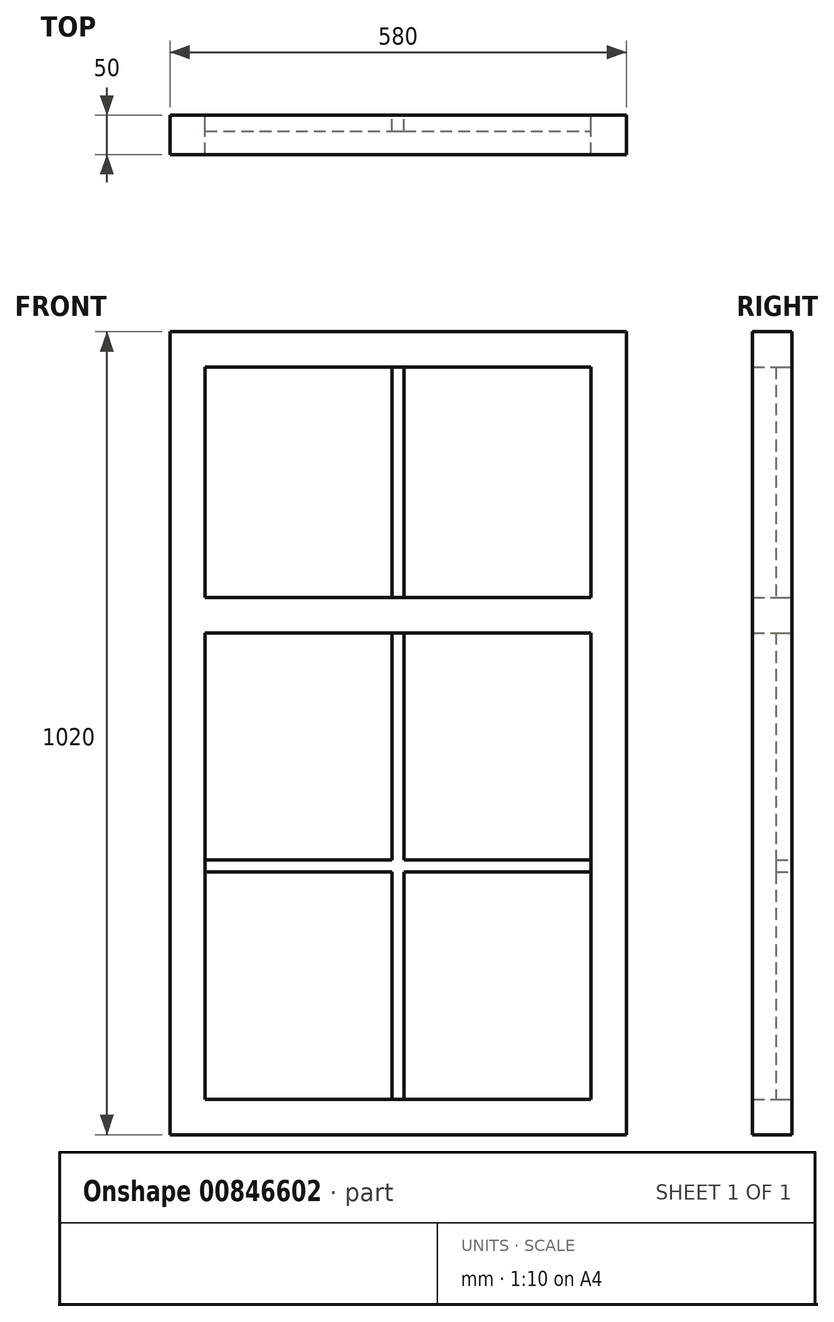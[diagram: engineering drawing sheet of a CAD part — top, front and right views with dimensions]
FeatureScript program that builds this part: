
annotation { "Feature Type Name" : "Feature", "Feature Type Description" : "" }
export const myFeature = defineFeature(function(context is Context, id is Id, definition is map)
    precondition{}
    {
        {
            var Q0;
            Q0=qCreatedBy(makeId("Front.planeOp"),FACE);
            var sketch = newSketch(context, id + "F0", { "sketchPlane" : qUnion([Q0])});
            skLineSegment(sketch, "E0.bottom", {"start": v(0, 0) * mm, "end": v(580, 0) * mm});
            skLineSegment(sketch, "E0.top", {"start": v(0, 1020) * mm, "end": v(580, 1020) * mm});
            skLineSegment(sketch, "E0.left", {"start": v(0, 0) * mm, "end": v(0, 1020) * mm});
            skLineSegment(sketch, "E0.right", {"start": v(580, 0) * mm, "end": v(580, 1020) * mm});
            skLineSegment(sketch, "E1.bottom", {"start": v(45, 975) * mm, "end": v(535, 975) * mm});
            skLineSegment(sketch, "E1.top", {"start": v(45, 45) * mm, "end": v(535, 45) * mm});
            skLineSegment(sketch, "E1.left", {"start": v(45, 975) * mm, "end": v(45, 682.5) * mm});
            skLineSegment(sketch, "E1.right", {"start": v(535, 975) * mm, "end": v(535, 682.5) * mm});
            skLineSegment(sketch, "E2.bottom", {"start": v(45, 682.5) * mm, "end": v(535, 682.5) * mm});
            skLineSegment(sketch, "E2.top", {"start": v(45, 637.5) * mm, "end": v(535, 637.5) * mm});
            skLineSegment(sketch, "E3.trimOffspring", {"start": v(535, 637.5) * mm, "end": v(535, 45) * mm});
            skLineSegment(sketch, "E4.trimOffspring", {"start": v(45, 637.5) * mm, "end": v(45, 45) * mm});
            skSolve(sketch);
        }
        {
            var Q0;
            Q0=qSketchRegion(id+"F0",true);
            extrude(context, id + "F1", {"entities" : qUnion([Q0]), "depth" : 50 * mm, "offsetDistance" : 25 * mm});
        }
        {
            var Q0;
            Q0=qCreatedBy(makeId("Front.planeOp"),FACE);
            var sketch = newSketch(context, id + "F2", { "sketchPlane" : qUnion([Q0])});
            skLineSegment(sketch, "E5.bottom", {"start": v(282.5, 975) * mm, "end": v(297.5, 975) * mm});
            skLineSegment(sketch, "E5.top", {"start": v(282.5, 682.5) * mm, "end": v(297.5, 682.5) * mm});
            skLineSegment(sketch, "E5.left", {"start": v(282.5, 975) * mm, "end": v(282.5, 682.5) * mm});
            skLineSegment(sketch, "E5.right", {"start": v(297.5, 975) * mm, "end": v(297.5, 682.5) * mm});
            skLineSegment(sketch, "E6.bottom", {"start": v(282.5, 637.5) * mm, "end": v(297.5, 637.5) * mm});
            skLineSegment(sketch, "E6.top", {"start": v(282.5, 45) * mm, "end": v(297.5, 45) * mm});
            skLineSegment(sketch, "E6.left", {"start": v(282.5, 637.5) * mm, "end": v(282.5, 348.75) * mm});
            skLineSegment(sketch, "E6.right", {"start": v(297.5, 637.5) * mm, "end": v(297.5, 348.75) * mm});
            skLineSegment(sketch, "E7.bottom", {"start": v(45, 348.75) * mm, "end": v(282.5, 348.75) * mm});
            skLineSegment(sketch, "E7.top", {"start": v(45, 333.75) * mm, "end": v(282.5, 333.75) * mm});
            skLineSegment(sketch, "E7.left", {"start": v(45, 348.75) * mm, "end": v(45, 333.75) * mm});
            skLineSegment(sketch, "E7.right", {"start": v(535, 348.75) * mm, "end": v(535, 333.75) * mm});
            skLineSegment(sketch, "E8.trimOffspring", {"start": v(297.5, 348.75) * mm, "end": v(535, 348.75) * mm});
            skLineSegment(sketch, "E9.trimOffspring", {"start": v(282.5, 333.75) * mm, "end": v(282.5, 45) * mm});
            skLineSegment(sketch, "E10.trimOffspring", {"start": v(297.5, 333.75) * mm, "end": v(535, 333.75) * mm});
            skLineSegment(sketch, "E11.trimOffspring", {"start": v(297.5, 333.75) * mm, "end": v(297.5, 45) * mm});
            skSolve(sketch);
        }
        {
            var Q0;
            Q0 = qSketchRegion(id + "F2", true);
            extrude(context, id + "F3", {"entities" : qUnion([Q0]), "operationType" : NewBodyOperationType.ADD, "depth" : 20 * mm, "offsetDistance" : 25 * mm});
        }
    });
